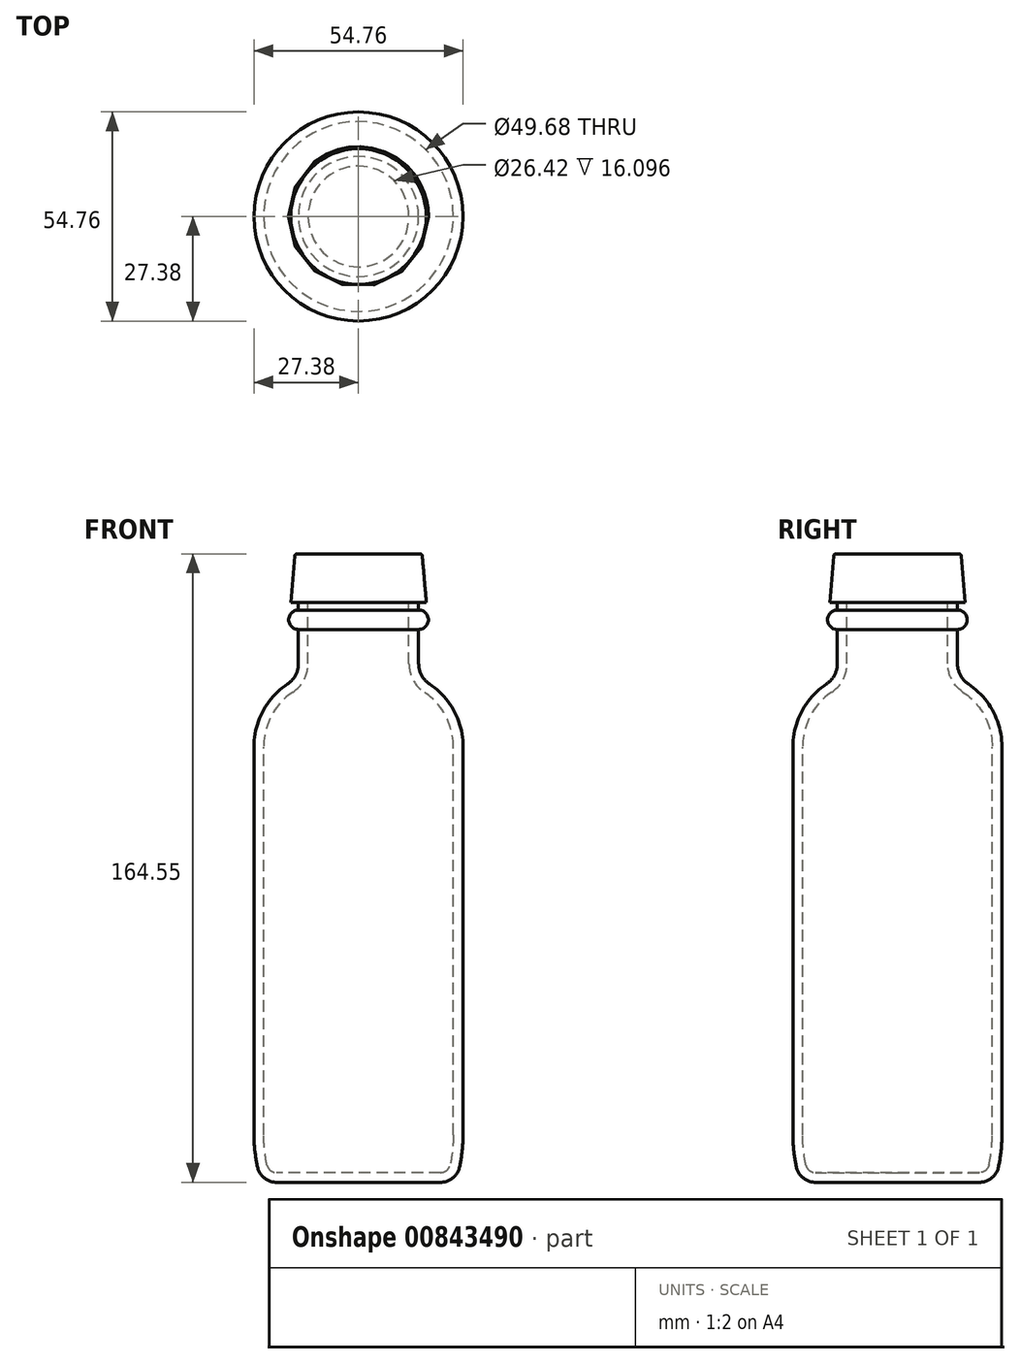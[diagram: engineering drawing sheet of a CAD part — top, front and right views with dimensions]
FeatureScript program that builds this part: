
annotation { "Feature Type Name" : "Feature", "Feature Type Description" : "" }
export const myFeature = defineFeature(function(context is Context, id is Id, definition is map)
    precondition{}
    {
        {
            var Q0;
            Q0=qCreatedBy(makeId("Front.planeOp"),FACE);
            var sketch = newSketch(context, id + "F0", { "sketchPlane" : qUnion([Q0])});
            skLineSegment(sketch, "E0", {"start": v(0, 0) * mm, "end": v(25.4, 0) * mm});
            skArc(sketch, "E1", {"start": v(25.4, 0) * mm, "mid": v(26.88, 6.15) * mm, "end": v(27.38, 12.46) * mm});
            skLineSegment(sketch, "E2", {"start": v(27.38, 12.46) * mm, "end": v(27.38, 114.06) * mm});
            skArc(sketch, "E3", {"start": v(27.38, 114.06) * mm, "mid": v(25.04, 123.4) * mm, "end": v(18.58, 130.51) * mm});
            skLineSegment(sketch, "E4", {"start": v(15.75, 135.8) * mm, "end": v(15.75, 144.78) * mm});
            skArc(sketch, "E5", {"start": v(15.75, 144.78) * mm, "mid": v(18.3, 147.32) * mm, "end": v(15.75, 149.86) * mm});
            skLineSegment(sketch, "E6", {"start": v(15.75, 149.86) * mm, "end": v(15.75, 152.4) * mm});
            skLineSegment(sketch, "E7", {"start": v(0, 152.4) * mm, "end": v(15.75, 152.4) * mm});
            skLineSegment(sketch, "E8", {"start": v(0, 152.4) * mm, "end": v(0, 0) * mm});
            skPoint(sketch, "E9.visualSharp", {"position": v(15.75, 132.08) * mm});
            skArc(sketch, "E9.filletArc", {"start": v(15.75, 135.8) * mm, "mid": v(16.5, 132.8) * mm, "end": v(18.58, 130.51) * mm});
            skSolve(sketch);
        }
        {
            var Q0;
            Q0=makeQuery(id+"F0.imprint","IMPRINT",FACE,{"disambiguationData":[TD([[makeQuery(id+"F0.imprint","IMPRINT",EDGE,{"derivedFrom":sQuery(id+"F0.wireOp",EDGE,"E0")}),1.0]])]});
            var Q1;
            Q1=sQuery(id+"F0.wireOp",EDGE,"E8");
            revolve(context, id + "F1", {"surfaceOperationType" : NewSurfaceOperationType.NEW, "entities" : qUnion([Q0]), "axis" : qUnion([Q1]), "revolveType" : RevolveType.FULL});
        }
        {
            var Q0;
            Q0=makeQuery(id+"F1.opRevolve","SWEPT_EDGE",EDGE,{"disambiguationData":[OSD([sQuery(id+"F0.wireOp",EDGE,"E0"),sQuery(id+"F0.wireOp",EDGE,"E1")])]});
            fillet(context, id + "F2", {"entities" : qUnion([Q0]), "radius" : 5.08 * mm, "tangentPropagation" : true, "allowEdgeOverflow" : false});
        }
        {
            var Q0;
            Q0=makeQuery(id+"F1.opRevolve","SWEPT_FACE",FACE,{"disambiguationData":[OSD([sQuery(id+"F0.wireOp",EDGE,"E7")])]});
            shell(context, id + "F3", {"entities" : qUnion([Q0]), "thickness" : 2.54 * mm});
        }
        {
            var Q0;
            Q0=qCreatedBy(makeId("Front.planeOp"),FACE);
            var sketch = newSketch(context, id + "F4", { "sketchPlane" : qUnion([Q0])});
            skLineSegment(sketch, "E10", {"start": v(0, 151.9) * mm, "end": v(17.75, 151.9) * mm});
            skLineSegment(sketch, "E11", {"start": v(17.75, 151.9) * mm, "end": v(16.67, 164.55) * mm});
            skLineSegment(sketch, "E12", {"start": v(16.67, 164.55) * mm, "end": v(0, 164.55) * mm});
            skLineSegment(sketch, "E13", {"start": v(0, 164.55) * mm, "end": v(0, 151.9) * mm});
            skSolve(sketch);
        }
        {
            var Q0;
            Q0=makeQuery(id+"F4.imprint","IMPRINT",FACE,{"disambiguationData":[TD([[makeQuery(id+"F4.imprint","IMPRINT",EDGE,{"derivedFrom":sQuery(id+"F4.wireOp",EDGE,"E10")}),1.0]])]});
            var Q1;
            Q1=sQuery(id+"F4.wireOp",EDGE,"E13");
            revolve(context, id + "F5", {"operationType" : NewBodyOperationType.ADD, "surfaceOperationType" : NewSurfaceOperationType.NEW, "entities" : qUnion([Q0]), "axis" : qUnion([Q1]), "revolveType" : RevolveType.FULL});
        }
        {
            var Q0;
            Q0=makeQuery(id+"F5.opRevolve","SWEPT_EDGE",EDGE,{"disambiguationData":[OSD([sQuery(id+"F4.wireOp",EDGE,"E11"),sQuery(id+"F4.wireOp",EDGE,"E12")])]});
            fillet(context, id + "F6", {"entities" : qUnion([Q0]), "radius" : 0.5 * mm, "tangentPropagation" : true, "allowEdgeOverflow" : false});
        }
    });
